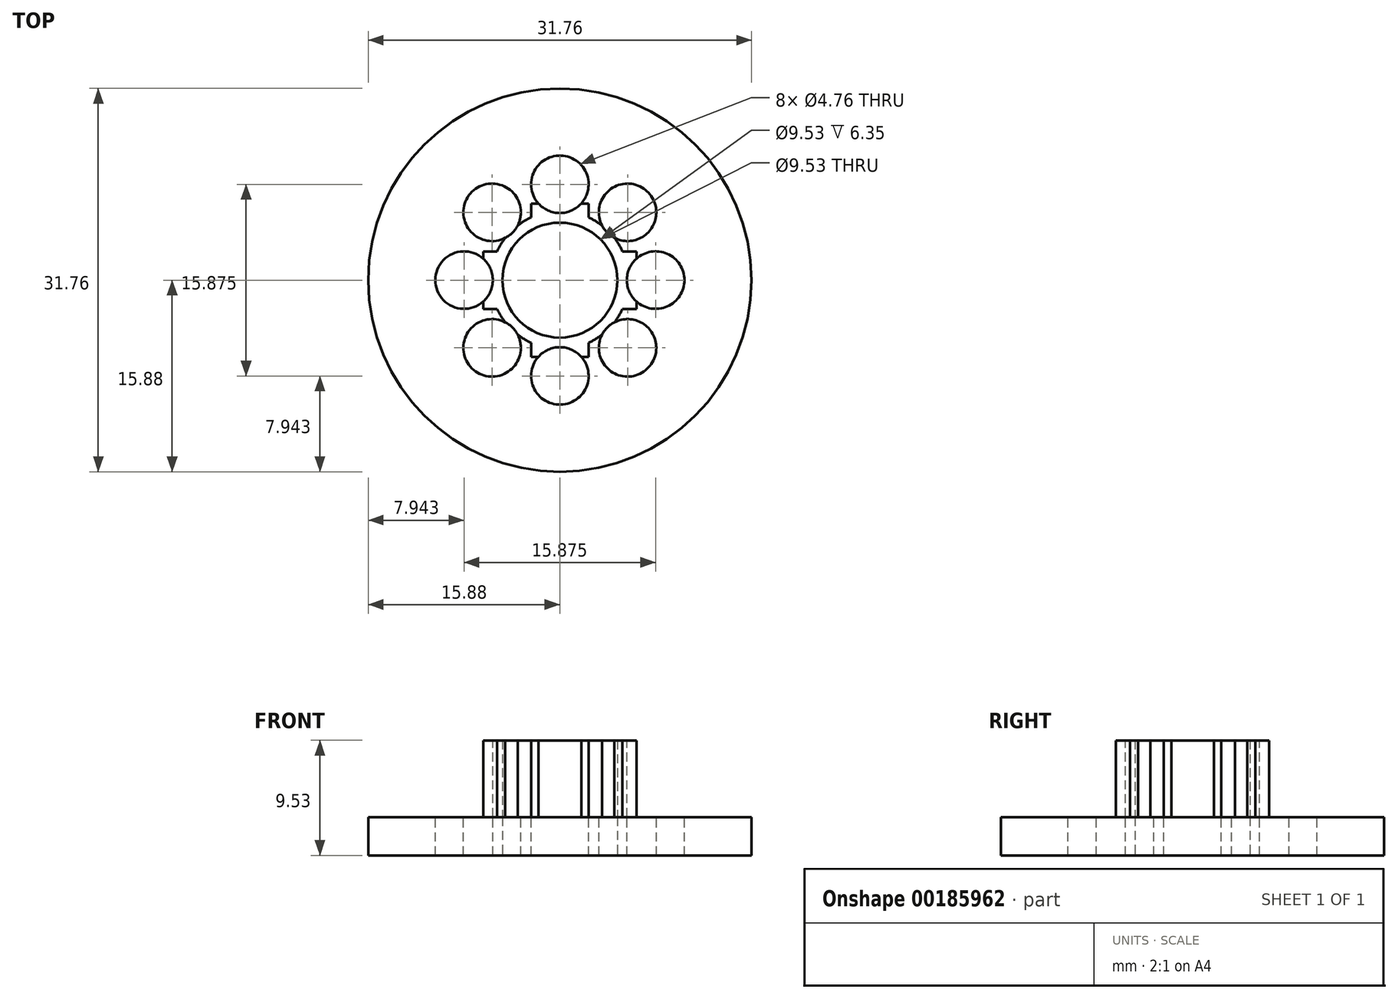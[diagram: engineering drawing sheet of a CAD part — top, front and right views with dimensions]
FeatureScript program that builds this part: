
annotation { "Feature Type Name" : "Feature", "Feature Type Description" : "" }
export const myFeature = defineFeature(function(context is Context, id is Id, definition is map)
    precondition{}
    {
        {
            var Q0;
            Q0=qCreatedBy(makeId("Top.planeOp"),FACE);
            var sketch = newSketch(context, id + "F0", { "sketchPlane" : qUnion([Q0])});
            skCircle(sketch, "E0", {"center": v(0, 0) * mm, "radius": 15.88 * mm});
            skCircle(sketch, "E1", {"center": v(0, 0) * mm, "radius": 4.76 * mm});
            skSolve(sketch);
        }
        {
            var Q0;
            Q0=qSketchRegion(id+"F0",true);
            extrude(context, id + "F1", {"entities" : qUnion([Q0]), "depth" : 3.17 * mm});
        }
        {
            var Q0;
            Q0=makeQuery(id+"F1.opExtrude","CAP_FACE",FACE,{"disambiguationData":[OSD([sQuery(id+"F0.wireOp",EDGE,"E0"),sQuery(id+"F0.wireOp",EDGE,"E1")])],"isStart":false});
            var sketch = newSketch(context, id + "F2", { "sketchPlane" : qUnion([Q0])});
            skCircle(sketch, "E2", {"center": v(0, 0) * mm, "radius": 4.76 * mm});
            skLineSegment(sketch, "E3.bottom", {"start": v(-2.38, 6.35) * mm, "end": v(2.38, 6.35) * mm});
            skLineSegment(sketch, "E3.top", {"start": v(-2.38, -6.35) * mm, "end": v(2.38, -6.35) * mm});
            skLineSegment(sketch, "E3.left", {"start": v(-2.38, 6.35) * mm, "end": v(-2.38, -6.35) * mm});
            skLineSegment(sketch, "E3.right", {"start": v(2.38, 6.35) * mm, "end": v(2.38, -6.35) * mm});
            skLineSegment(sketch, "E4.bottom", {"start": v(-6.35, 2.38) * mm, "end": v(6.35, 2.38) * mm});
            skLineSegment(sketch, "E4.top", {"start": v(-6.35, -2.38) * mm, "end": v(6.35, -2.38) * mm});
            skLineSegment(sketch, "E4.left", {"start": v(-6.35, 2.38) * mm, "end": v(-6.35, -2.38) * mm});
            skLineSegment(sketch, "E4.right", {"start": v(6.35, 2.38) * mm, "end": v(6.35, -2.38) * mm});
            skCircle(sketch, "E5", {"center": v(0, 0) * mm, "radius": 5.72 * mm});
            skSolve(sketch);
        }
        {
            var Q0;
            {var subQ5=sQuery(id+"F2.wireOp",EDGE,"E3.bottom");Q0=makeQuery(id+"F2.imprint","IMPRINT",FACE,{"disambiguationData":[TD([[makeQuery(id+"F2.imprint","IMPRINT",EDGE,{"derivedFrom":subQ5}),-1.0]])]});}
            var Q1;
            {var subQ5=sQuery(id+"F2.wireOp",EDGE,"E3.top");Q1=makeQuery(id+"F2.imprint","IMPRINT",FACE,{"disambiguationData":[TD([[makeQuery(id+"F2.imprint","IMPRINT",EDGE,{"derivedFrom":subQ5}),1.0]])]});}
            var Q2;
            {var subQ5=sQuery(id+"F2.wireOp",EDGE,"E4.right");Q2=makeQuery(id+"F2.imprint","IMPRINT",FACE,{"disambiguationData":[TD([[makeQuery(id+"F2.imprint","IMPRINT",EDGE,{"derivedFrom":subQ5}),-1.0]])]});}
            var Q3;
            {var subQ0=sQuery(id+"F2.wireOp",EDGE,"E3.left");var subQ1=sQuery(id+"F2.wireOp",EDGE,"E2");var subQ2=makeQuery(id+"F2.imprint","INTERSECT",VERTEX,{"disambiguationData":[OD(0.0)],"derivedFrom":[subQ1,subQ0]});Q3=makeQuery(id+"F2.imprint","IMPRINT",FACE,{"disambiguationData":[TD([[makeQuery(id+"F2.imprint","IMPRINT",EDGE,{"disambiguationData":[TD([[subQ2,-1.0]])],"derivedFrom":subQ1}),-1.0]])]});}
            var Q4;
            {var subQ0=sQuery(id+"F2.wireOp",EDGE,"E3.right");var subQ1=sQuery(id+"F2.wireOp",EDGE,"E2");var subQ2=makeQuery(id+"F2.imprint","INTERSECT",VERTEX,{"disambiguationData":[OD(0.0)],"derivedFrom":[subQ1,subQ0]});Q4=makeQuery(id+"F2.imprint","IMPRINT",FACE,{"disambiguationData":[TD([[makeQuery(id+"F2.imprint","IMPRINT",EDGE,{"disambiguationData":[TD([[subQ2,-1.0]])],"derivedFrom":subQ1}),-1.0]])]});}
            var Q5;
            {var subQ0=sQuery(id+"F2.wireOp",EDGE,"E3.right");var subQ1=sQuery(id+"F2.wireOp",EDGE,"E2");var subQ2=makeQuery(id+"F2.imprint","INTERSECT",VERTEX,{"disambiguationData":[OD(0.0)],"derivedFrom":[subQ1,subQ0]});Q5=makeQuery(id+"F2.imprint","IMPRINT",FACE,{"disambiguationData":[TD([[makeQuery(id+"F2.imprint","IMPRINT",EDGE,{"disambiguationData":[TD([[subQ2,1.0]])],"derivedFrom":subQ1}),-1.0]])]});}
            var Q6;
            {var subQ0=sQuery(id+"F2.wireOp",EDGE,"E4.bottom");var subQ1=sQuery(id+"F2.wireOp",EDGE,"E2");var subQ2=makeQuery(id+"F2.imprint","INTERSECT",VERTEX,{"disambiguationData":[OD(0.0)],"derivedFrom":[subQ1,subQ0]});Q6=makeQuery(id+"F2.imprint","IMPRINT",FACE,{"disambiguationData":[TD([[makeQuery(id+"F2.imprint","IMPRINT",EDGE,{"disambiguationData":[TD([[subQ2,1.0]])],"derivedFrom":subQ1}),-1.0]])]});}
            var Q7;
            {var subQ0=sQuery(id+"F2.wireOp",EDGE,"E3.right");var subQ1=sQuery(id+"F2.wireOp",EDGE,"E2");var subQ2=makeQuery(id+"F2.imprint","INTERSECT",VERTEX,{"disambiguationData":[OD(1.0)],"derivedFrom":[subQ1,subQ0]});Q7=makeQuery(id+"F2.imprint","IMPRINT",FACE,{"disambiguationData":[TD([[makeQuery(id+"F2.imprint","IMPRINT",EDGE,{"disambiguationData":[TD([[subQ2,-1.0]])],"derivedFrom":subQ1}),-1.0]])]});}
            var Q8;
            {var subQ0=sQuery(id+"F2.wireOp",EDGE,"E3.left");var subQ1=sQuery(id+"F2.wireOp",EDGE,"E2");var subQ2=makeQuery(id+"F2.imprint","INTERSECT",VERTEX,{"disambiguationData":[OD(1.0)],"derivedFrom":[subQ1,subQ0]});Q8=makeQuery(id+"F2.imprint","IMPRINT",FACE,{"disambiguationData":[TD([[makeQuery(id+"F2.imprint","IMPRINT",EDGE,{"disambiguationData":[TD([[subQ2,-1.0]])],"derivedFrom":subQ1}),-1.0]])]});}
            var Q9;
            {var subQ0=sQuery(id+"F2.wireOp",EDGE,"E4.top");var subQ1=sQuery(id+"F2.wireOp",EDGE,"E2");var subQ2=makeQuery(id+"F2.imprint","INTERSECT",VERTEX,{"disambiguationData":[OD(0.0)],"derivedFrom":[subQ1,subQ0]});Q9=makeQuery(id+"F2.imprint","IMPRINT",FACE,{"disambiguationData":[TD([[makeQuery(id+"F2.imprint","IMPRINT",EDGE,{"disambiguationData":[TD([[subQ2,-1.0]])],"derivedFrom":subQ1}),-1.0]])]});}
            var Q10;
            {var subQ0=sQuery(id+"F2.wireOp",EDGE,"E4.bottom");var subQ1=sQuery(id+"F2.wireOp",EDGE,"E2");var subQ2=makeQuery(id+"F2.imprint","INTERSECT",VERTEX,{"disambiguationData":[OD(1.0)],"derivedFrom":[subQ1,subQ0]});Q10=makeQuery(id+"F2.imprint","IMPRINT",FACE,{"disambiguationData":[TD([[makeQuery(id+"F2.imprint","IMPRINT",EDGE,{"disambiguationData":[TD([[subQ2,-1.0]])],"derivedFrom":subQ1}),-1.0]])]});}
            var Q11;
            {var subQ0=sQuery(id+"F2.wireOp",EDGE,"E4.left");Q11=makeQuery(id+"F2.imprint","IMPRINT",FACE,{"disambiguationData":[TD([[makeQuery(id+"F2.imprint","IMPRINT",EDGE,{"derivedFrom":subQ0}),1.0]])]});}
            extrude(context, id + "F3", {"entities" : qUnion([Q0, Q1, Q2, Q3, Q4, Q5, Q6, Q7, Q8, Q9, Q10, Q11]), "depth" : 6.35 * mm});
        }
        {
            var Q0;
            Q0=makeQuery(id+"F3.opExtrude","CAP_FACE",FACE,{"disambiguationData":[OSD([sQuery(id+"F2.wireOp",EDGE,"E2"),sQuery(id+"F2.wireOp",EDGE,"E3.bottom"),sQuery(id+"F2.wireOp",EDGE,"E3.top"),sQuery(id+"F2.wireOp",EDGE,"E3.left"),sQuery(id+"F2.wireOp",EDGE,"E3.right"),sQuery(id+"F2.wireOp",EDGE,"E4.bottom"),sQuery(id+"F2.wireOp",EDGE,"E4.top"),sQuery(id+"F2.wireOp",EDGE,"E4.left"),sQuery(id+"F2.wireOp",EDGE,"E4.right")])],"isStart":false});
            var sketch = newSketch(context, id + "F4", { "sketchPlane" : qUnion([Q0])});
            skCircle(sketch, "E6", {"center": v(0, 0) * mm, "radius": 15.88 * mm});
            skCircle(sketch, "E7", {"center": v(0, 0) * mm, "radius": 4.76 * mm});
            skSolve(sketch);
        }
        {
            var Q0;
            Q0=qSketchRegion(id+"F4",true);
            extrude(context, id + "F5", {"entities" : qUnion([Q0]), "operationType" : NewBodyOperationType.ADD, "depth" : 3.17 * mm});
        }
        {
            var Q0;
            Q0=makeQuery(id+"F5.opExtrude","CAP_FACE",FACE,{"disambiguationData":[OSD([sQuery(id+"F4.wireOp",EDGE,"E6"),sQuery(id+"F4.wireOp",EDGE,"E7")])],"isStart":false});
            var sketch = newSketch(context, id + "F6", { "sketchPlane" : qUnion([Q0])});
            skCircle(sketch, "E8", {"center": v(0, 7.94) * mm, "radius": 2.38 * mm});
            skCircle(sketch, "E9.1.0", {"center": v(-5.61, 5.61) * mm, "radius": 2.38 * mm});
            skCircle(sketch, "E9.2.0", {"center": v(-7.94, 0) * mm, "radius": 2.38 * mm});
            skCircle(sketch, "E9.3.0", {"center": v(-5.61, -5.61) * mm, "radius": 2.38 * mm});
            skCircle(sketch, "E9.4.0", {"center": v(0, -7.94) * mm, "radius": 2.38 * mm});
            skCircle(sketch, "E9.5.0", {"center": v(5.61, -5.61) * mm, "radius": 2.38 * mm});
            skCircle(sketch, "E9.6.0", {"center": v(7.94, 0) * mm, "radius": 2.38 * mm});
            skCircle(sketch, "E9.7.0", {"center": v(5.61, 5.61) * mm, "radius": 2.38 * mm});
            skPoint(sketch, "E9.center", {"position": v(0, 0) * mm});
            skSolve(sketch);
        }
        {
            var Q0;
            Q0=makeQuery(id+"F6.imprint","IMPRINT",FACE,{"disambiguationData":[TD([[makeQuery(id+"F6.imprint","IMPRINT",EDGE,{"derivedFrom":sQuery(id+"F6.wireOp",EDGE,"E9.1.0")}),1.0]])]});
            var Q1;
            Q1=makeQuery(id+"F6.imprint","IMPRINT",FACE,{"disambiguationData":[TD([[makeQuery(id+"F6.imprint","IMPRINT",EDGE,{"derivedFrom":sQuery(id+"F6.wireOp",EDGE,"E9.5.0")}),1.0]])]});
            var Q2;
            Q2=makeQuery(id+"F6.imprint","IMPRINT",FACE,{"disambiguationData":[TD([[makeQuery(id+"F6.imprint","IMPRINT",EDGE,{"derivedFrom":sQuery(id+"F6.wireOp",EDGE,"E8")}),1.0]])]});
            var Q3;
            Q3=makeQuery(id+"F6.imprint","IMPRINT",FACE,{"disambiguationData":[TD([[makeQuery(id+"F6.imprint","IMPRINT",EDGE,{"derivedFrom":sQuery(id+"F6.wireOp",EDGE,"E9.7.0")}),1.0]])]});
            var Q4;
            Q4=makeQuery(id+"F6.imprint","IMPRINT",FACE,{"disambiguationData":[TD([[makeQuery(id+"F6.imprint","IMPRINT",EDGE,{"derivedFrom":sQuery(id+"F6.wireOp",EDGE,"E9.6.0")}),1.0]])]});
            var Q5;
            Q5=makeQuery(id+"F6.imprint","IMPRINT",FACE,{"disambiguationData":[TD([[makeQuery(id+"F6.imprint","IMPRINT",EDGE,{"derivedFrom":sQuery(id+"F6.wireOp",EDGE,"E9.4.0")}),1.0]])]});
            var Q6;
            Q6=makeQuery(id+"F6.imprint","IMPRINT",FACE,{"disambiguationData":[TD([[makeQuery(id+"F6.imprint","IMPRINT",EDGE,{"derivedFrom":sQuery(id+"F6.wireOp",EDGE,"E9.3.0")}),1.0]])]});
            var Q7;
            Q7=makeQuery(id+"F6.imprint","IMPRINT",FACE,{"disambiguationData":[TD([[makeQuery(id+"F6.imprint","IMPRINT",EDGE,{"derivedFrom":sQuery(id+"F6.wireOp",EDGE,"E9.2.0")}),1.0]])]});
            extrude(context, id + "F7", {"entities" : qUnion([Q0, Q1, Q2, Q3, Q4, Q5, Q6, Q7]), "operationType" : NewBodyOperationType.REMOVE, "oppositeDirection" : true, "depth" : 25.4 * mm});
        }
        {
            var Q0;
            Q0=makeQuery(id+"F1.opExtrude","CAP_FACE",FACE,{"disambiguationData":[OSD([sQuery(id+"F0.wireOp",EDGE,"E0"),sQuery(id+"F0.wireOp",EDGE,"E1")])],"isStart":true});
            var sketch = newSketch(context, id + "F8", { "sketchPlane" : qUnion([Q0])});
            skCircle(sketch, "E10", {"center": v(0, 7.94) * mm, "radius": 1.59 * mm});
            skCircle(sketch, "E11.1.0", {"center": v(-5.61, 5.61) * mm, "radius": 1.59 * mm});
            skCircle(sketch, "E11.2.0", {"center": v(-7.94, 0) * mm, "radius": 1.59 * mm});
            skCircle(sketch, "E11.3.0", {"center": v(-5.61, -5.61) * mm, "radius": 1.59 * mm});
            skCircle(sketch, "E11.4.0", {"center": v(0, -7.94) * mm, "radius": 1.59 * mm});
            skCircle(sketch, "E11.5.0", {"center": v(5.61, -5.61) * mm, "radius": 1.59 * mm});
            skCircle(sketch, "E11.6.0", {"center": v(7.94, 0) * mm, "radius": 1.59 * mm});
            skCircle(sketch, "E11.7.0", {"center": v(5.61, 5.61) * mm, "radius": 1.59 * mm});
            skPoint(sketch, "E11.center", {"position": v(0, 0) * mm});
            skSolve(sketch);
        }
        {
            var Q0;
            Q0=makeQuery(id+"F8.imprint","IMPRINT",FACE,{"disambiguationData":[TD([[makeQuery(id+"F8.imprint","IMPRINT",EDGE,{"derivedFrom":sQuery(id+"F8.wireOp",EDGE,"E10")}),-1.0]])]});
            var Q1;
            Q1=makeQuery(id+"F8.imprint","IMPRINT",FACE,{"disambiguationData":[TD([[makeQuery(id+"F8.imprint","IMPRINT",EDGE,{"derivedFrom":sQuery(id+"F8.wireOp",EDGE,"E11.7.0")}),-1.0]])]});
            var Q2;
            Q2=makeQuery(id+"F8.imprint","IMPRINT",FACE,{"disambiguationData":[TD([[makeQuery(id+"F8.imprint","IMPRINT",EDGE,{"derivedFrom":sQuery(id+"F8.wireOp",EDGE,"E11.6.0")}),-1.0]])]});
            var Q3;
            Q3=makeQuery(id+"F8.imprint","IMPRINT",FACE,{"disambiguationData":[TD([[makeQuery(id+"F8.imprint","IMPRINT",EDGE,{"derivedFrom":sQuery(id+"F8.wireOp",EDGE,"E11.5.0")}),-1.0]])]});
            var Q4;
            Q4=makeQuery(id+"F8.imprint","IMPRINT",FACE,{"disambiguationData":[TD([[makeQuery(id+"F8.imprint","IMPRINT",EDGE,{"derivedFrom":sQuery(id+"F8.wireOp",EDGE,"E11.4.0")}),-1.0]])]});
            var Q5;
            Q5=makeQuery(id+"F8.imprint","IMPRINT",FACE,{"disambiguationData":[TD([[makeQuery(id+"F8.imprint","IMPRINT",EDGE,{"derivedFrom":sQuery(id+"F8.wireOp",EDGE,"E11.3.0")}),-1.0]])]});
            var Q6;
            Q6=makeQuery(id+"F8.imprint","IMPRINT",FACE,{"disambiguationData":[TD([[makeQuery(id+"F8.imprint","IMPRINT",EDGE,{"derivedFrom":sQuery(id+"F8.wireOp",EDGE,"E11.2.0")}),-1.0]])]});
            var Q7;
            Q7=makeQuery(id+"F8.imprint","IMPRINT",FACE,{"disambiguationData":[TD([[makeQuery(id+"F8.imprint","IMPRINT",EDGE,{"derivedFrom":sQuery(id+"F8.wireOp",EDGE,"E11.1.0")}),-1.0]])]});
            var Q8;
            Q8=makeQuery(id+"F8.imprint","IMPRINT",FACE,{"disambiguationData":[TD([[makeQuery(id+"F8.imprint","IMPRINT",EDGE,{"derivedFrom":sQuery(id+"F8.wireOp",EDGE,"E11.6.0")}),1.0]])]});
            var Q9;
            Q9=makeQuery(id+"F8.imprint","IMPRINT",FACE,{"disambiguationData":[TD([[makeQuery(id+"F8.imprint","IMPRINT",EDGE,{"derivedFrom":sQuery(id+"F8.wireOp",EDGE,"E11.5.0")}),1.0]])]});
            var Q10;
            Q10=makeQuery(id+"F8.imprint","IMPRINT",FACE,{"disambiguationData":[TD([[makeQuery(id+"F8.imprint","IMPRINT",EDGE,{"derivedFrom":sQuery(id+"F8.wireOp",EDGE,"E11.4.0")}),1.0]])]});
            var Q11;
            Q11=makeQuery(id+"F8.imprint","IMPRINT",FACE,{"disambiguationData":[TD([[makeQuery(id+"F8.imprint","IMPRINT",EDGE,{"derivedFrom":sQuery(id+"F8.wireOp",EDGE,"E11.3.0")}),1.0]])]});
            var Q12;
            Q12=makeQuery(id+"F8.imprint","IMPRINT",FACE,{"disambiguationData":[TD([[makeQuery(id+"F8.imprint","IMPRINT",EDGE,{"derivedFrom":sQuery(id+"F8.wireOp",EDGE,"E11.2.0")}),1.0]])]});
            var Q13;
            Q13=makeQuery(id+"F8.imprint","IMPRINT",FACE,{"disambiguationData":[TD([[makeQuery(id+"F8.imprint","IMPRINT",EDGE,{"derivedFrom":sQuery(id+"F8.wireOp",EDGE,"E11.1.0")}),1.0]])]});
            var Q14;
            Q14=makeQuery(id+"F8.imprint","IMPRINT",FACE,{"disambiguationData":[TD([[makeQuery(id+"F8.imprint","IMPRINT",EDGE,{"derivedFrom":sQuery(id+"F8.wireOp",EDGE,"E10")}),1.0]])]});
            var Q15;
            Q15=makeQuery(id+"F8.imprint","IMPRINT",FACE,{"disambiguationData":[TD([[makeQuery(id+"F8.imprint","IMPRINT",EDGE,{"derivedFrom":sQuery(id+"F8.wireOp",EDGE,"E11.7.0")}),1.0]])]});
            extrude(context, id + "F9", {"entities" : qUnion([Q0, Q1, Q2, Q3, Q4, Q5, Q6, Q7, Q8, Q9, Q10, Q11, Q12, Q13, Q14, Q15]), "operationType" : NewBodyOperationType.REMOVE, "oppositeDirection" : true, "depth" : 25.4 * mm});
        }
        {
            var Q0;
            Q0=makeQuery(id+"F5.opExtrude","CAP_FACE",FACE,{"disambiguationData":[OSD([sQuery(id+"F4.wireOp",EDGE,"E6"),sQuery(id+"F4.wireOp",EDGE,"E7")])],"isStart":false});
            extrude(context, id + "F10", {"entities" : qUnion([Q0]), "operationType" : NewBodyOperationType.REMOVE, "oppositeDirection" : true, "depth" : 3.17 * mm});
        }
    });
